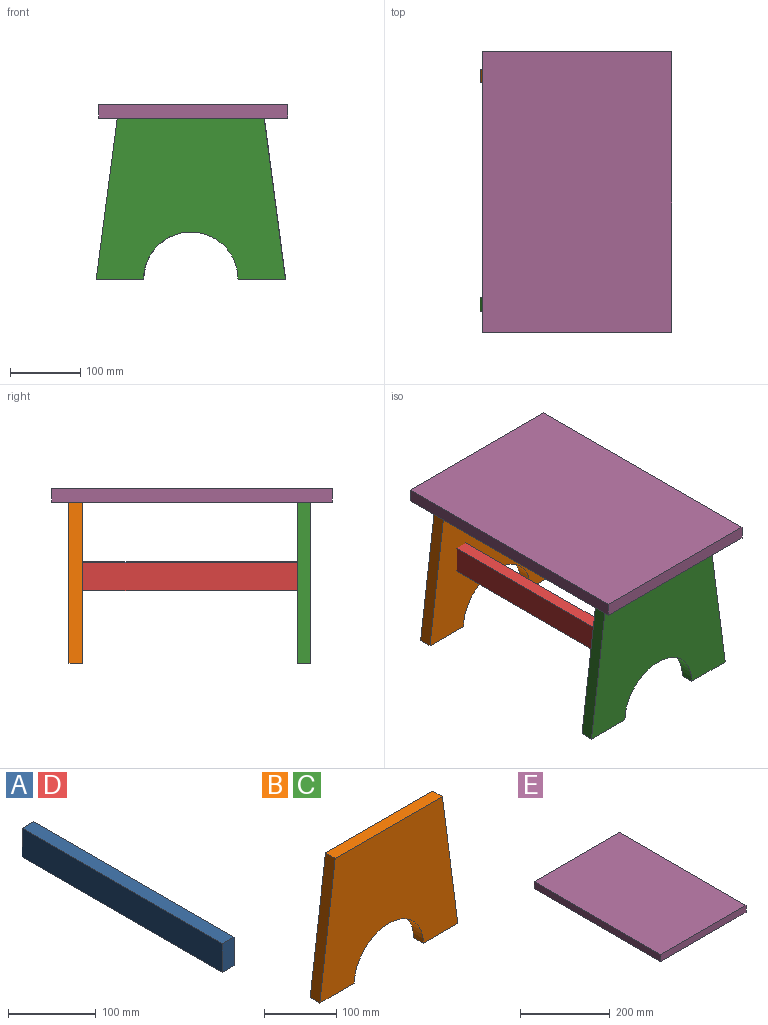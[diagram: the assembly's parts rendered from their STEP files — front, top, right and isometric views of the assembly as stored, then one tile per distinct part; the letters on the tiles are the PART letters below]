
ASSEMBLY  parts=5 mates=4
PART A: 6 faces, bbox 19x322x40 mm
  f0: plane 322x19mm, normal (0,0,1), area 6118mm2, adj f1,f3,f4,f5
  f1: plane 40x19mm, normal (0,-1,0), area 760mm2, adj f0,f2,f4,f5
  f2: plane 322x19mm, normal (0,0,-1), area 6118mm2, adj f1,f3,f4,f5
  f3: plane 40x19mm, normal (0,1,0), area 760mm2, adj f0,f2,f4,f5
  f4: plane 322x40mm, normal (1,0,0), area 12880mm2, adj f0,f1,f2,f3
  f5: plane 322x40mm, normal (-1,0,0), area 12880mm2, adj f0,f1,f2,f3
PART B: 8 faces, bbox 270x19x230 mm
  f0: plane 209.69x19mm, normal (0,0,1), area 3984mm2, adj f1,f5,f6,f7
  f1: plane 230x30.01mm, normal (-0.99,0,0.13), area 4407mm2, adj f0,f2,f6,f7
  f2: plane 67.6x19mm, normal (0,0,-1), area 1284.4mm2, adj f1,f3,f6,f7
  f3: cylinder r=67.4mm len=134.8mm, axis (0,1,0), area 4023.2mm2, adj f2,f4,f6,f7
  f4: plane 67.6x19mm, normal (0,0,-1), area 1284.4mm2, adj f3,f5,f6,f7
  f5: plane 230x30.31mm, normal (0.99,0,0.13), area 4407.8mm2, adj f0,f4,f6,f7
  f6: plane 270x230mm, normal (0,-1,0), area 48027.9mm2, adj f0,f1,f2,f3,f4,f5
  f7: plane 270x230mm, normal (0,1,0), area 48027.9mm2, adj f0,f1,f2,f3,f4,f5
PART C: same geometry as B
PART D: same geometry as A
PART E: 6 faces, bbox 270x400x19 mm
  f0: plane 270x19mm, normal (0,1,0), area 5130mm2, adj f1,f3,f4,f5
  f1: plane 400x19mm, normal (-1,0,0), area 7600mm2, adj f0,f2,f4,f5
  f2: plane 270x19mm, normal (0,-1,0), area 5130mm2, adj f1,f3,f4,f5
  f3: plane 400x19mm, normal (1,0,0), area 7600mm2, adj f0,f2,f4,f5
  f4: plane 400x270mm, normal (0,0,1), area 108000mm2, adj f0,f1,f2,f3
  f5: plane 400x270mm, normal (0,0,-1), area 108000mm2, adj f0,f1,f2,f3
PLACE A t=(-51.78,107.88,126.76)mm
PLACE B t=(-87.95,285.2,76.45)mm
PLACE C t=(-88.35,-40.89,76.45)mm
PLACE D t=(-197.46,107.88,125.49)mm
PLACE E t=(-106.45,-3.4,239.06)mm
MATE planar A.f1 <-> C.f7  axis (0,-1,0) through (-42.28,-40.89,133.97)mm
MATE planar C.f0 <-> E.f5  axis (0,0,1) through (-116.48,-50.39,239.06)mm
MATE planar B.f0 <-> E.f5  axis (0,0,1) through (-116.08,275.7,239.06)mm
MATE planar D.f1 <-> C.f7  axis (0,-1,0) through (-187.96,-40.89,132.7)mm
